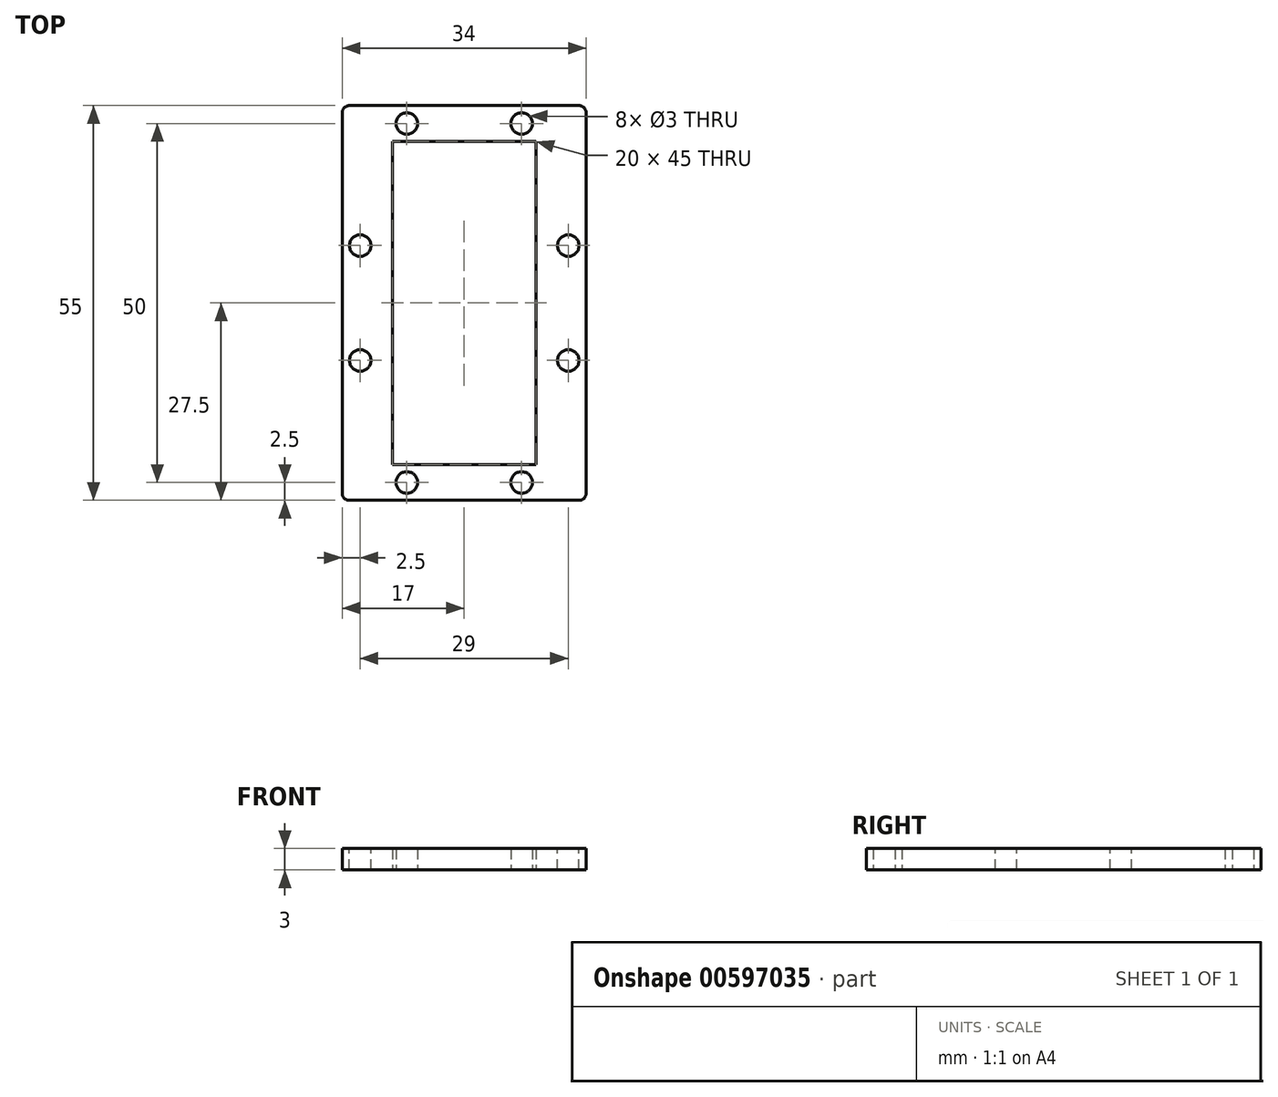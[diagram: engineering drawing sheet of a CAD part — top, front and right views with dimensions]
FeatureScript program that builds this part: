
annotation { "Feature Type Name" : "Feature", "Feature Type Description" : "" }
export const myFeature = defineFeature(function(context is Context, id is Id, definition is map)
    precondition{}
    {
        {
            var Q0;
            Q0=qCreatedBy(makeId("Top.planeOp"),FACE);
            var sketch = newSketch(context, id + "F0", { "sketchPlane" : qUnion([Q0])});
            skLineSegment(sketch, "E0.bottom", {"start": v(17, 27.5) * mm, "end": v(-17, 27.5) * mm});
            skLineSegment(sketch, "E0.top", {"start": v(17, -27.5) * mm, "end": v(-17, -27.5) * mm});
            skLineSegment(sketch, "E0.left", {"start": v(17, 27.5) * mm, "end": v(17, -27.5) * mm});
            skLineSegment(sketch, "E0.right", {"start": v(-17, 27.5) * mm, "end": v(-17, -27.5) * mm});
            skPoint(sketch, "E0.middle", {"position": v(0, 0) * mm});
            skLineSegment(sketch, "E1.bottom", {"start": v(10, 22.5) * mm, "end": v(-10, 22.5) * mm});
            skLineSegment(sketch, "E1.top", {"start": v(10, -22.5) * mm, "end": v(-10, -22.5) * mm});
            skLineSegment(sketch, "E1.left", {"start": v(10, 22.5) * mm, "end": v(10, -22.5) * mm});
            skLineSegment(sketch, "E1.right", {"start": v(-10, 22.5) * mm, "end": v(-10, -22.5) * mm});
            skLineSegment(sketch, "E2", {"start": v(0, 27.5) * mm, "end": v(0, -27.5) * mm, "construction": true});
            skLineSegment(sketch, "E3", {"start": v(-17, 0) * mm, "end": v(17, 0) * mm, "construction": true});
            skCircle(sketch, "E4", {"center": v(-8, 25) * mm, "radius": 1.5 * mm});
            skLineSegment(sketch, "E5.MirrorCS", {"start": v(17, 0) * mm, "end": v(-17, 0) * mm, "construction": true});
            skCircle(sketch, "E6.MirrorC", {"center": v(8, 25) * mm, "radius": 1.5 * mm});
            skCircle(sketch, "E7.MirrorC", {"center": v(-8, -25) * mm, "radius": 1.5 * mm});
            skCircle(sketch, "E8.MirrorC", {"center": v(8, -25) * mm, "radius": 1.5 * mm});
            skSolve(sketch);
        }
        {
            var Q0;
            Q0=makeQuery(id+"F0.imprint","IMPRINT",FACE,{"disambiguationData":[TD([[makeQuery(id+"F0.imprint","IMPRINT",EDGE,{"derivedFrom":sQuery(id+"F0.wireOp",EDGE,"E0.bottom")}),1.0]])]});
            extrude(context, id + "F1", {"entities" : qUnion([Q0]), "depth" : 3 * mm, "offsetDistance" : 25.4 * mm});
        }
        {
            var Q0;
            Q0=makeQuery(id+"F1.opExtrude","CAP_FACE",FACE,{"disambiguationData":[OSD([sQuery(id+"F0.wireOp",EDGE,"E0.bottom"),sQuery(id+"F0.wireOp",EDGE,"E0.top"),sQuery(id+"F0.wireOp",EDGE,"E0.left"),sQuery(id+"F0.wireOp",EDGE,"E0.right"),sQuery(id+"F0.wireOp",EDGE,"E1.bottom"),sQuery(id+"F0.wireOp",EDGE,"E1.top"),sQuery(id+"F0.wireOp",EDGE,"E1.left"),sQuery(id+"F0.wireOp",EDGE,"E1.right"),sQuery(id+"F0.wireOp",EDGE,"E4"),sQuery(id+"F0.wireOp",EDGE,"E6.MirrorC"),sQuery(id+"F0.wireOp",EDGE,"E7.MirrorC"),sQuery(id+"F0.wireOp",EDGE,"E8.MirrorC")])],"isStart":false});
            var sketch = newSketch(context, id + "F2", { "sketchPlane" : qUnion([Q0])});
            skLineSegment(sketch, "E9", {"start": v(-17, 0) * mm, "end": v(17, 0) * mm, "construction": true});
            skCircle(sketch, "E10", {"center": v(-14.5, 8) * mm, "radius": 1.5 * mm});
            skLineSegment(sketch, "E11", {"start": v(0, 27.5) * mm, "end": v(0, -27.5) * mm, "construction": true});
            skCircle(sketch, "E12.MirrorC", {"center": v(14.5, 8) * mm, "radius": 1.5 * mm});
            skCircle(sketch, "E13.MirrorC", {"center": v(-14.5, -8) * mm, "radius": 1.5 * mm});
            skCircle(sketch, "E14.MirrorC", {"center": v(14.5, -8) * mm, "radius": 1.5 * mm});
            skSolve(sketch);
        }
        {
            var Q0;
            Q0 = qSketchRegion(id + "F2", true);
            extrude(context, id + "F3", {"entities" : qUnion([Q0]), "operationType" : NewBodyOperationType.REMOVE, "oppositeDirection" : true, "depth" : 5 * mm, "offsetDistance" : 25.4 * mm});
        }
        {
            var Q0;
            Q0=makeQuery(id+"F1.opExtrude","SWEPT_EDGE",EDGE,{"disambiguationData":[OSD([sQuery(id+"F0.wireOp",EDGE,"E0.bottom"),sQuery(id+"F0.wireOp",EDGE,"E0.right")])]});
            var Q1;
            Q1=makeQuery(id+"F1.opExtrude","SWEPT_EDGE",EDGE,{"disambiguationData":[OSD([sQuery(id+"F0.wireOp",EDGE,"E0.bottom"),sQuery(id+"F0.wireOp",EDGE,"E0.left")])]});
            var Q2;
            Q2=makeQuery(id+"F1.opExtrude","SWEPT_EDGE",EDGE,{"disambiguationData":[OSD([sQuery(id+"F0.wireOp",EDGE,"E0.top"),sQuery(id+"F0.wireOp",EDGE,"E0.left")])]});
            var Q3;
            Q3=makeQuery(id+"F1.opExtrude","SWEPT_EDGE",EDGE,{"disambiguationData":[OSD([sQuery(id+"F0.wireOp",EDGE,"E0.top"),sQuery(id+"F0.wireOp",EDGE,"E0.right")])]});
            fillet(context, id + "F4", {"entities" : qUnion([Q0, Q1, Q2, Q3]), "radius" : 1 * mm, "tangentPropagation" : true, "allowEdgeOverflow" : false});
        }
    });
